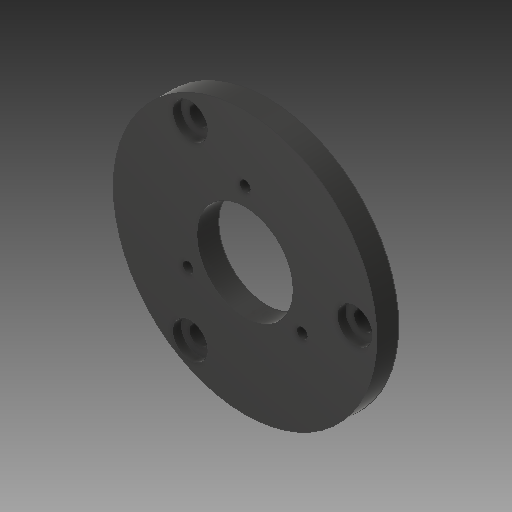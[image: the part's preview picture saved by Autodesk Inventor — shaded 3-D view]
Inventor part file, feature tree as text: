
AUTODESK INVENTOR PART (.ipt)
format: ipt  version: 2018 (Build 220112000, 112)  size: 276,480 bytes
history: native  units: in
note: dims shown in document units (in); Inventor stores cm internally (conversion verified against a paired STEP export)
features: sketch x3, extrude x2, hole x1, pattern_circular x1
ambient origin geometry x8: Origin, YZ Plane, XZ Plane, XY Plane, X Axis, Y Axis, Z Axis, Center Point
bodies: Solid1 (feature_tree)
feature tree (7):
  extrude  "Extrusion1"  Depth=2.3622in
  hole  "Hole1"  [1 undecoded]
  pattern_circular  "Circular Pattern2"  [2 undecoded]
  extrude  "Extrusion8"  Depth=0.3937in TaperAngle=0.0deg
  sketch  "Sketch1"  dims[d0=0.7874in d1=2.3622in]
  sketch  "Sketch4"  dims[d3=0.0984in d4=1.1811in d6=360.0deg]
  sketch  "Sketch5"  dims[d8=0.1969in d9=0.0in d34=0.0394in d35=0.3937in d36=0.0in d40=1.9685in d41=0.1772in d42=0.1772in d43=0.2362in d44=0.315in d45=0.0787in d46=90.0deg d47=0.315in d48=0.8108in d49=1.1811in d50=360.0deg]
note: 3 required parameter values undecoded (feature->parameter linkage not recoverable at this tier; creation-order binding heuristic only, values carry confidence <= 0.55)
